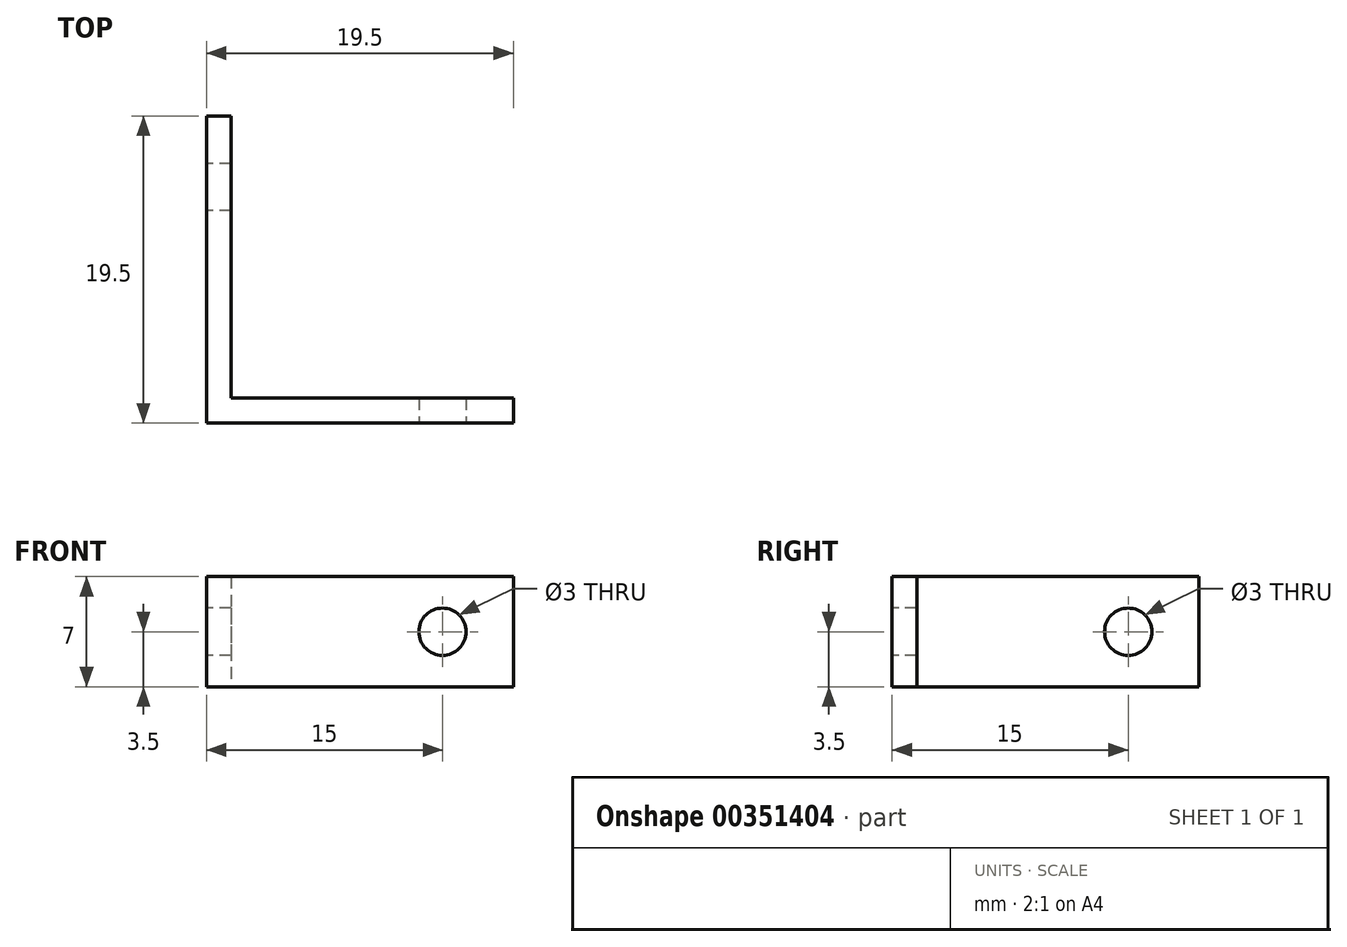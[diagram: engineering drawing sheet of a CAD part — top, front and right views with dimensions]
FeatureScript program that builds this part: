
annotation { "Feature Type Name" : "Feature", "Feature Type Description" : "" }
export const myFeature = defineFeature(function(context is Context, id is Id, definition is map)
    precondition{}
    {
        {
            var Q0;
            Q0=qCreatedBy(makeId("Top.planeOp"),FACE);
            var sketch = newSketch(context, id + "F0", { "sketchPlane" : qUnion([Q0])});
            skLineSegment(sketch, "E0.bottom", {"start": v(0, 0) * mm, "end": v(1.58, 0) * mm});
            skLineSegment(sketch, "E0.top", {"start": v(0, 25.42) * mm, "end": v(1.58, 25.42) * mm});
            skLineSegment(sketch, "E0.left", {"start": v(0, 0) * mm, "end": v(0, 25.42) * mm});
            skLineSegment(sketch, "E0.right", {"start": v(1.58, 0) * mm, "end": v(1.58, 25.42) * mm});
            skLineSegment(sketch, "E1.bottom", {"start": v(1.58, 0) * mm, "end": v(25.42, 0) * mm});
            skLineSegment(sketch, "E1.top", {"start": v(1.58, 1.58) * mm, "end": v(25.42, 1.58) * mm});
            skLineSegment(sketch, "E1.left", {"start": v(1.58, 0) * mm, "end": v(1.58, 1.58) * mm});
            skLineSegment(sketch, "E1.right", {"start": v(25.42, 0) * mm, "end": v(25.42, 1.58) * mm});
            skSolve(sketch);
        }
        {
            var Q0;
            Q0=qSketchRegion(id+"F0",true);
            extrude(context, id + "F1", {"entities" : qUnion([Q0]), "depth" : 7 * mm});
        }
        {
            var Q0;
            Q0=makeQuery(id+"F1.opExtrude","SWEPT_FACE",FACE,{"disambiguationData":[OSD([sQuery(id+"F0.wireOp",EDGE,"E0.left")])]});
            var sketch = newSketch(context, id + "F2", { "sketchPlane" : qUnion([Q0])});
            skCircle(sketch, "E2", {"center": v(-15, 3.5) * mm, "radius": 1.5 * mm});
            skLineSegment(sketch, "E3.bottom", {"start": v(-25.42, 7) * mm, "end": v(-19.5, 7) * mm});
            skLineSegment(sketch, "E3.top", {"start": v(-25.42, 0) * mm, "end": v(-19.5, 0) * mm});
            skLineSegment(sketch, "E3.left", {"start": v(-25.42, 7) * mm, "end": v(-25.42, 0) * mm});
            skLineSegment(sketch, "E3.right", {"start": v(-19.5, 7) * mm, "end": v(-19.5, 0) * mm});
            skSolve(sketch);
        }
        {
            var Q0;
            Q0=qSketchRegion(id+"F2",true);
            extrude(context, id + "F3", {"entities" : qUnion([Q0]), "operationType" : NewBodyOperationType.REMOVE, "oppositeDirection" : true, "depth" : 25 * mm});
        }
        {
            var Q0;
            Q0=makeQuery(id+"F1.opExtrude","SWEPT_FACE",FACE,{"disambiguationData":[OSD([sQuery(id+"F0.wireOp",EDGE,"E0.bottom"),sQuery(id+"F0.wireOp",EDGE,"E1.bottom")])]});
            var sketch = newSketch(context, id + "F4", { "sketchPlane" : qUnion([Q0])});
            skCircle(sketch, "E4", {"center": v(15, 3.5) * mm, "radius": 1.5 * mm});
            skLineSegment(sketch, "E5.bottom", {"start": v(25.42, 7) * mm, "end": v(19.5, 7) * mm});
            skLineSegment(sketch, "E5.top", {"start": v(25.42, 0) * mm, "end": v(19.5, 0) * mm});
            skLineSegment(sketch, "E5.left", {"start": v(25.42, 7) * mm, "end": v(25.42, 0) * mm});
            skLineSegment(sketch, "E5.right", {"start": v(19.5, 7) * mm, "end": v(19.5, 0) * mm});
            skSolve(sketch);
        }
        {
            var Q0;
            Q0=qSketchRegion(id+"F4",true);
            extrude(context, id + "F5", {"entities" : qUnion([Q0]), "operationType" : NewBodyOperationType.REMOVE, "oppositeDirection" : true, "depth" : 25 * mm});
        }
    });
